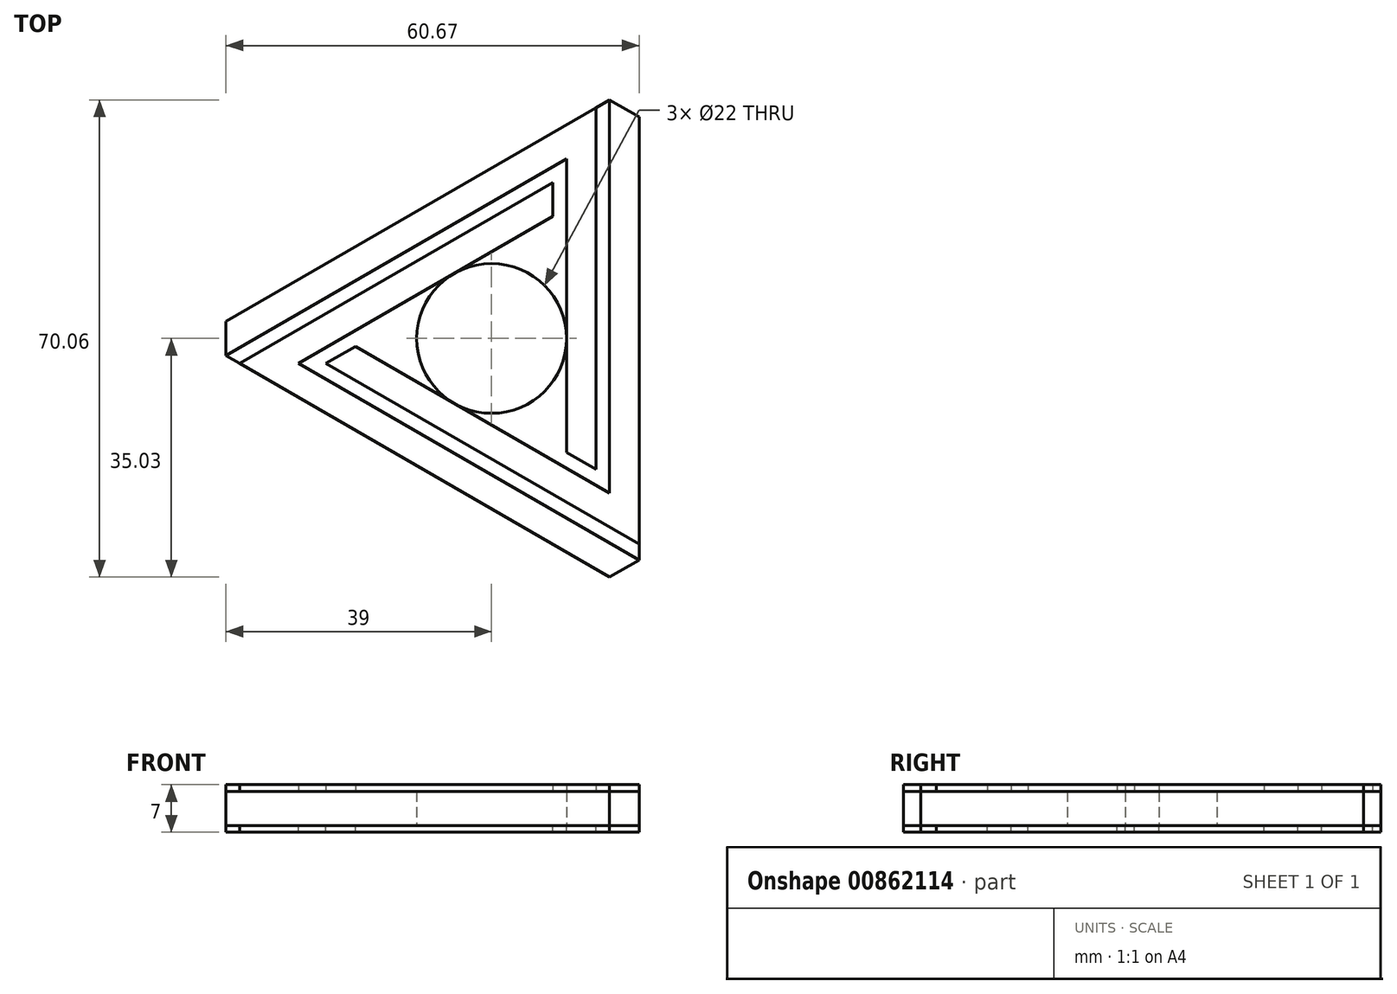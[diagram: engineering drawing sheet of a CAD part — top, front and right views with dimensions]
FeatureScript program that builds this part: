
annotation { "Feature Type Name" : "Feature", "Feature Type Description" : "" }
export const myFeature = defineFeature(function(context is Context, id is Id, definition is map)
    precondition{}
    {
        {
            var Q0;
            Q0=qCreatedBy(makeId("Top.planeOp"),FACE);
            var sketch = newSketch(context, id + "F0", { "sketchPlane" : qUnion([Q0])});
            skCircle(sketch, "E0.cCircle", {"center": v(0, 0) * mm, "radius": 21.67 * mm, "construction": true});
            skLineSegment(sketch, "E0.0", {"start": v(21.67, 37.53) * mm, "end": v(21.67, -37.53) * mm});
            skLineSegment(sketch, "E0.1", {"start": v(21.67, -37.53) * mm, "end": v(-43.33, 0) * mm});
            skLineSegment(sketch, "E0.2", {"start": v(-43.33, 0) * mm, "end": v(21.67, 37.53) * mm});
            skPoint(sketch, "E0.0.midPoint", {"position": v(21.67, 0) * mm});
            skCircle(sketch, "E1", {"center": v(0, 0) * mm, "radius": 11 * mm});
            skPoint(sketch, "E2", {"position": v(-39, 2.5) * mm});
            skPoint(sketch, "E3", {"position": v(-39, -2.5) * mm});
            skLineSegment(sketch, "E4", {"start": v(-39, 2.5) * mm, "end": v(-39, -2.5) * mm});
            skLineSegment(sketch, "E5.1.0", {"start": v(17.34, -35.03) * mm, "end": v(21.67, -32.53) * mm});
            skLineSegment(sketch, "E5.2.0", {"start": v(21.67, 32.53) * mm, "end": v(17.34, 35.03) * mm});
            skSolve(sketch);
        }
        {
            var Q0;
            Q0=makeQuery(id+"F0.imprint","IMPRINT",FACE,{"disambiguationData":[TD([[makeQuery(id+"F0.imprint","IMPRINT",EDGE,{"derivedFrom":sQuery(id+"F0.wireOp",EDGE,"E1")}),-1.0]])]});
            extrude(context, id + "F1", {"entities" : qUnion([Q0]), "endBound" : BoundingType.SYMMETRIC, "depth" : 5 * mm, "offsetDistance" : 25 * mm});
        }
        {
            var Q0;
            Q0=makeQuery(id+"F1.opExtrude","CAP_FACE",FACE,{"disambiguationData":[OSD([sQuery(id+"F0.wireOp",EDGE,"E0.0"),sQuery(id+"F0.wireOp",EDGE,"E0.1"),sQuery(id+"F0.wireOp",EDGE,"E0.2"),sQuery(id+"F0.wireOp",EDGE,"E1"),sQuery(id+"F0.wireOp",EDGE,"E4"),sQuery(id+"F0.wireOp",EDGE,"E5.1.0"),sQuery(id+"F0.wireOp",EDGE,"E5.2.0")])],"isStart":false});
            var sketch = newSketch(context, id + "F2", { "sketchPlane" : qUnion([Q0])});
            skLineSegment(sketch, "E6", {"start": v(-39, -2.5) * mm, "end": v(11, 26.37) * mm});
            skLineSegment(sketch, "E7", {"start": v(17.34, 35.03) * mm, "end": v(17.34, -22.71) * mm});
            skLineSegment(sketch, "E8", {"start": v(21.67, -32.53) * mm, "end": v(-28.34, -3.66) * mm});
            skLineSegment(sketch, "E9", {"start": v(-28.34, -3.66) * mm, "end": v(11, 19.05) * mm});
            skLineSegment(sketch, "E10", {"start": v(17.34, -22.71) * mm, "end": v(-22, 0) * mm});
            skLineSegment(sketch, "E11", {"start": v(11, 26.37) * mm, "end": v(11, -19.05) * mm});
            skLineSegment(sketch, "E12", {"start": v(-37, -3.66) * mm, "end": v(9, 22.9) * mm});
            skLineSegment(sketch, "E13", {"start": v(9, 22.9) * mm, "end": v(9, 17.9) * mm});
            skSolve(sketch);
        }
        {
            var Q0;
            {var subQ4=sQuery(id+"F2.wireOp",EDGE,"E8");Q0=makeQuery(id+"F2.imprint","IMPRINT",FACE,{"disambiguationData":[TD([[makeQuery(id+"F2.imprint","IMPRINT",EDGE,{"derivedFrom":subQ4}),1.0]])]});}
            extrude(context, id + "F3", {"entities" : qUnion([Q0]), "depth" : 1 * mm, "offsetDistance" : 25 * mm});
        }
        {
            var Q0;
            Q0=qCreatedBy(makeId("Right.planeOp"),FACE);
            var sketch = newSketch(context, id + "F4", { "sketchPlane" : qUnion([Q0])});
            skLineSegment(sketch, "E14", {"start": v(0, 46.04) * mm, "end": v(0, -28.87) * mm});
            skSolve(sketch);
        }
        {
            var Q0;
            Q0=makeQuery(id+"F3.opExtrude","SWEPT_BODY",BODY,{"disambiguationData":[OSD([sQuery(id+"F0.wireOp",EDGE,"E0.1"),sQuery(id+"F0.wireOp",EDGE,"E5.1.0"),sQuery(id+"F2.wireOp",EDGE,"E8"),sQuery(id+"F2.wireOp",EDGE,"E9"),sQuery(id+"F2.wireOp",EDGE,"E12"),sQuery(id+"F2.wireOp",EDGE,"E13")])]});
            var Q1;
            Q1=makeQuery(id+"F1.opExtrude","SWEPT_BODY",BODY,{"disambiguationData":[OSD([sQuery(id+"F0.wireOp",EDGE,"E0.0"),sQuery(id+"F0.wireOp",EDGE,"E0.1"),sQuery(id+"F0.wireOp",EDGE,"E0.2"),sQuery(id+"F0.wireOp",EDGE,"E1"),sQuery(id+"F0.wireOp",EDGE,"E4"),sQuery(id+"F0.wireOp",EDGE,"E5.1.0"),sQuery(id+"F0.wireOp",EDGE,"E5.2.0")])]});
            var Q2;
            Q2=sQuery(id+"F4.wireOp",EDGE,"E14");
            circularPattern(context, id + "F5", {"entities" : qUnion([Q0, Q1]), "axis" : qUnion([Q2]), "angle" : 360 * degree, "instanceCount" : 3, "equalSpace" : true});
        }
        {
            var Q0;
            Q0=makeQuery(id+"F5.opPattern","COPY",BODY,{"derivedFrom":makeQuery(id+"F3.opExtrude","SWEPT_BODY",BODY,{"disambiguationData":[OSD([sQuery(id+"F0.wireOp",EDGE,"E0.1"),sQuery(id+"F0.wireOp",EDGE,"E5.1.0"),sQuery(id+"F2.wireOp",EDGE,"E8"),sQuery(id+"F2.wireOp",EDGE,"E9"),sQuery(id+"F2.wireOp",EDGE,"E12"),sQuery(id+"F2.wireOp",EDGE,"E13")])]}),"instanceName":"1"});
            var Q1;
            Q1=makeQuery(id+"F3.opExtrude","SWEPT_BODY",BODY,{"disambiguationData":[OSD([sQuery(id+"F0.wireOp",EDGE,"E0.1"),sQuery(id+"F0.wireOp",EDGE,"E5.1.0"),sQuery(id+"F2.wireOp",EDGE,"E8"),sQuery(id+"F2.wireOp",EDGE,"E9"),sQuery(id+"F2.wireOp",EDGE,"E12"),sQuery(id+"F2.wireOp",EDGE,"E13")])]});
            var Q2;
            Q2=makeQuery(id+"F5.opPattern","COPY",BODY,{"derivedFrom":makeQuery(id+"F3.opExtrude","SWEPT_BODY",BODY,{"disambiguationData":[OSD([sQuery(id+"F0.wireOp",EDGE,"E0.1"),sQuery(id+"F0.wireOp",EDGE,"E5.1.0"),sQuery(id+"F2.wireOp",EDGE,"E8"),sQuery(id+"F2.wireOp",EDGE,"E9"),sQuery(id+"F2.wireOp",EDGE,"E12"),sQuery(id+"F2.wireOp",EDGE,"E13")])]}),"instanceName":"2"});
            var Q3;
            Q3=qCreatedBy(makeId("Top.planeOp"),FACE);
            mirror(context, id + "F6", {"entities" : qUnion([Q0, Q1, Q2]), "mirrorPlane" : qUnion([Q3])});
        }
    });
